# Revit family: HermanMiller_Seating_Verus_WorkChairUpholsteredBack
name_source: partatom
category: Furniture
revit_build: Autodesk Revit Architecture 2014 (Build: 20130308_1515(x64)
units: mm (PartAtom-declared; Revit-internal decimal feet)

## types (96) — shared parameters
Assembly Code = E2020200
Manufacturer = Herman Miller, Inc.
Package Qty = 1
URL = http://www.hermanmiller.com
zero-valued in all types: PosOpt

## per-type parameters (varying)
| type | Adj Arms | Arm Type | Arms | Description | Fixed Arms | Height Adjustable | Model | Sync |
| Low-Hgt Range Adj Wgt Act w/Tlt Lim Fully Adj Arms Adj Seat Depth | Yes | 2 | Yes | Wk Task Chr Verus Uphst Back Low-Hgt Range Adj Weight Activated w/Tlt Lim Fully Adj Arms Adj Seat Depth | No | Yes | PI1B215AA | No |
| Low-Hgt Range Adj Wgt Act w/Tlt Lim Fully Adj Arms Adj Seat Depth FR | Yes | 2 | Yes | Wk Task Chr Verus Uphst Back Low-Hgt Range Adj Weight Activated w/Tlt Lim Fully Adj Arms Adj Seat Depth FR | No | Yes | PI1B215AAFR | No |
| Low-Hgt Range Adj Wgt Act w/Tlt Lim Fully Adj Arms Fxd Seat Depth | Yes | 2 | Yes | Wk Task Chr Verus Uphst Back Low-Hgt Range Adj Weight Activated w/Tlt Lim Fully Adj Arms Fixed Seat Depth | No | Yes | PI1B215AF | No |
| Low-Hgt Range Adj Wgt Act w/Tlt Lim Fully Adj Arms Fxd Seat Depth FR | Yes | 2 | Yes | Wk Task Chr Verus Uphst Back Low-Hgt Range Adj Weight Activated w/Tlt Lim Fully Adj Arms Fixed Seat Depth FR | No | Yes | PI1B215AFFR | No |
| Low-Hgt Range Adj Wgt Act w/Tlt Lim Hgt Adj Arms Adj Seat Depth | Yes | 2 | Yes | Wk Task Chr Verus Uphst Back Low-Hgt Range Adj Weight Activated w/Tlt Lim Hgt Adj Arms Adj Seat Depth | No | Yes | PI1B215HA | No |
| Low-Hgt Range Adj Wgt Act w/Tlt Lim Hgt Adj Arms Adj Seat Depth FR | Yes | 2 | Yes | Wk Task Chr Verus Uphst Back Low-Hgt Range Adj Weight Activated w/Tlt Lim Hgt Adj Arms Adj Seat Depth FR | No | Yes | PI1B215HAFR | No |
| Low-Hgt Range Adj Wgt Act w/Tlt Lim Hgt Adj Arms Fxd Seat Depth | Yes | 2 | Yes | Wk Task Chr Verus Uphst Back Low-Hgt Range Adj Weight Activated w/Tlt Lim Hgt Adj Arms Fixed Seat Depth | No | Yes | PI1B215HF | No |
| Low-Hgt Range Adj Wgt Act w/Tlt Lim Hgt Adj Arms Fxd Seat Depth FR | Yes | 2 | Yes | Wk Task Chr Verus Uphst Back Low-Hgt Range Adj Weight Activated w/Tlt Lim Hgt Adj Arms Fixed Seat Depth FR | No | Yes | PI1B215HFFR | No |
| Low-Hgt Range Adj Wgt Act w/Tlt Lim No Arms Adj Seat Depth | No | 0 | No | Wk Task Chr Verus Uphst Back Low-Hgt Range Adj Weight Activated w/Tlt Lim No Arms Adj Seat Depth | No | Yes | PI1B215NA | No |
| Low-Hgt Range Adj Wgt Act w/Tlt Lim No Arms Adj Seat Depth FR | No | 0 | No | Wk Task Chr Verus Uphst Back Low-Hgt Range Adj Weight Activated w/Tlt Lim No Arms Adj Seat Depth FR | No | Yes | PI1B215NAFR | No |
| Low-Hgt Range Adj Wgt Act w/Tlt Lim No Arms Fxd Seat Depth | No | 0 | No | Wk Task Chr Verus Uphst Back Low-Hgt Range Adj Weight Activated w/Tlt Lim No Arms Fixed Seat Depth | No | Yes | PI1B215NF | No |
| Low-Hgt Range Adj Wgt Act w/Tlt Lim No Arms Fxd Seat Depth FR | No | 0 | No | Wk Task Chr Verus Uphst Back Low-Hgt Range Adj Weight Activated w/Tlt Lim No Arms Fixed Seat Depth FR | No | Yes | PI1B215NFFR | No |
| Low-Hgt Range Adj Wgt Act w/Tlt Lim Fxd Arms Adj Seat Depth | No | 1 | Yes | Wk Task Chr Verus Uphst Back Low-Hgt Range Adj Weight Activated w/Tlt Lim Fixed Arms Adj Seat Depth | Yes | Yes | PI1B215PA | No |
| Low-Hgt Range Adj Wgt Act w/Tlt Lim Fxd Arms Adj Seat Depth FR | No | 1 | Yes | Wk Task Chr Verus Uphst Back Low-Hgt Range Adj Weight Activated w/Tlt Lim Fixed Arms Adj Seat Depth FR | Yes | Yes | PI1B215PAFR | No |
| Low-Hgt Range Adj Wgt Act w/Tlt Lim Fxd Arms Fxd Seat Depth | No | 1 | Yes | Wk Task Chr Verus Uphst Back Low-Hgt Range Adj Weight Activated w/Tlt Lim Fixed Arms Fixed Seat Depth | Yes | Yes | PI1B215PF | No |
| Low-Hgt Range Adj Wgt Act w/Tlt Lim Fxd Arms Fxd Seat Depth FR | No | 1 | Yes | Wk Task Chr Verus Uphst Back Low-Hgt Range Adj Weight Activated w/Tlt Lim Fixed Arms Fixed Seat Depth FR | Yes | Yes | PI1B215PFFR | No |
| Low-Hgt Range Adj Sync w/Tlt Lim Fully Adj Arms Adj Seat Depth | Yes | 2 | Yes | Wk Task Chr Verus Uphst Back Low-Hgt Range Adj Synchronous w/Tlt Lim Fully Adj Arms Adj Seat Depth | No | No | PI1B216AA | Yes |
| Low-Hgt Range Adj Sync w/Tlt Lim Fully Adj Arms Adj Seat Depth FR | Yes | 2 | Yes | Wk Task Chr Verus Uphst Back Low-Hgt Range Adj Synchronous w/Tlt Lim Fully Adj Arms Adj Seat Depth FR | No | No | PI1B216AAFR | Yes |
| Low-Hgt Range Adj Sync w/Tlt Lim Fully Adj Arms Fxd Seat Depth | Yes | 2 | Yes | Wk Task Chr Verus Uphst Back Low-Hgt Range Adj Synchronous w/Tlt Lim Fully Adj Arms Fixed Seat Depth | No | No | PI1B216AF | Yes |
| Low-Hgt Range Adj Sync w/Tlt Lim Fully Adj Arms Fxd Seat Depth FR | Yes | 2 | Yes | Wk Task Chr Verus Uphst Back Low-Hgt Range Adj Synchronous w/Tlt Lim Fully Adj Arms Fixed Seat Depth FR | No | No | PI1B216AFFR | Yes |
| Low-Hgt Range Adj Sync w/Tlt Lim Hgt Adj Arms Adj Seat Depth | Yes | 2 | Yes | Wk Task Chr Verus Uphst Back Low-Hgt Range Adj Synchronous w/Tlt Lim Hgt Adj Arms Adj Seat Depth | No | No | PI1B216HA | Yes |
| Low-Hgt Range Adj Sync w/Tlt Lim Hgt Adj Arms Adj Seat Depth FR | Yes | 2 | Yes | Wk Task Chr Verus Uphst Back Low-Hgt Range Adj Synchronous w/Tlt Lim Hgt Adj Arms Adj Seat Depth FR | No | No | PI1B216HAFR | Yes |
| Low-Hgt Range Adj Sync w/Tlt Lim Hgt Adj Arms Fxd Seat Depth | Yes | 2 | Yes | Wk Task Chr Verus Uphst Back Low-Hgt Range Adj Synchronous w/Tlt Lim Hgt Adj Arms Fixed Seat Depth | No | No | PI1B216HF | Yes |
| Low-Hgt Range Adj Sync w/Tlt Lim Hgt Adj Arms Fxd Seat Depth FR | Yes | 2 | Yes | Wk Task Chr Verus Uphst Back Low-Hgt Range Adj Synchronous w/Tlt Lim Hgt Adj Arms Fixed Seat Depth FR | No | No | PI1B216HFFR | Yes |
| Low-Hgt Range Adj Sync w/Tlt Lim No Arms Adj Seat Depth | No | 0 | No | Wk Task Chr Verus Uphst Back Low-Hgt Range Adj Synchronous w/Tlt Lim No Arms Adj Seat Depth | No | No | PI1B216NA | Yes |
| Low-Hgt Range Adj Sync w/Tlt Lim No Arms Adj Seat Depth FR | No | 0 | No | Wk Task Chr Verus Uphst Back Low-Hgt Range Adj Synchronous w/Tlt Lim No Arms Adj Seat Depth FR | No | No | PI1B216NAFR | Yes |
| Low-Hgt Range Adj Sync w/Tlt Lim No Arms Fxd Seat Depth | No | 0 | No | Wk Task Chr Verus Uphst Back Low-Hgt Range Adj Synchronous w/Tlt Lim No Arms Fixed Seat Depth | No | No | PI1B216NF | Yes |
| Low-Hgt Range Adj Sync w/Tlt Lim No Arms Fxd Seat Depth FR | No | 0 | No | Wk Task Chr Verus Uphst Back Low-Hgt Range Adj Synchronous w/Tlt Lim No Arms Fixed Seat Depth FR | No | No | PI1B216NFFR | Yes |
| Low-Hgt Range Adj Sync w/Tlt Lim Fxd Arms Adj Seat Depth | No | 1 | Yes | Wk Task Chr Verus Uphst Back Low-Hgt Range Adj Synchronous w/Tlt Lim Fixed Arms Adj Seat Depth | Yes | No | PI1B216PA | Yes |
| Low-Hgt Range Adj Sync w/Tlt Lim Fxd Arms Adj Seat Depth FR | No | 1 | Yes | Wk Task Chr Verus Uphst Back Low-Hgt Range Adj Synchronous w/Tlt Lim Fixed Arms Adj Seat Depth FR | Yes | No | PI1B216PAFR | Yes |
| Low-Hgt Range Adj Sync w/Tlt Lim Fxd Arms Fxd Seat Depth | No | 1 | Yes | Wk Task Chr Verus Uphst Back Low-Hgt Range Adj Synchronous w/Tlt Lim Fixed Arms Fixed Seat Depth | Yes | No | PI1B216PF | Yes |
| Low-Hgt Range Adj Sync w/Tlt Lim Fxd Arms Fxd Seat Depth FR | No | 1 | Yes | Wk Task Chr Verus Uphst Back Low-Hgt Range Adj Synchronous w/Tlt Lim Fixed Arms Fixed Seat Depth FR | Yes | No | PI1B216PFFR | Yes |
| Low-Hgt Range Adj Sync w/Tlt Lim and Seat Angle Fully Adj Arms Adj Seat Depth | Yes | 2 | Yes | Wk Task Chr Verus Uphst Back Low-Hgt Range Adj Synchronous w/Tlt Lim and Seat Angle Fully Adj Arms Adj Seat Depth | No | No | PI1B217AA | Yes |
| Low-Hgt Range Adj Sync w/Tlt Lim and Seat Angle Fully Adj Arms Adj Seat Depth FR | Yes | 2 | Yes | Wk Task Chr Verus Uphst Back Low-Hgt Range Adj Synchronous w/Tlt Lim and Seat Angle Fully Adj Arms Adj Seat Depth FR | No | No | PI1B217AAFR | Yes |
| Low-Hgt Range Adj Sync w/Tlt Lim and Seat Angle Fully Adj Arms Fxd Seat Depth | Yes | 2 | Yes | Wk Task Chr Verus Uphst Back Low-Hgt Range Adj Synchronous w/Tlt Lim and Seat Angle Fully Adj Arms Fixed Seat Depth | No | No | PI1B217AF | Yes |
| Low-Hgt Range Adj Sync w/Tlt Lim and Seat Angle Fully Adj Arms Fxd Seat Depth FR | Yes | 2 | Yes | Wk Task Chr Verus Uphst Back Low-Hgt Range Adj Synchronous w/Tlt Lim and Seat Angle Fully Adj Arms Fixed Seat Depth FR | No | No | PI1B217AFFR | Yes |
| Low-Hgt Range Adj Sync w/Tlt Lim and Seat Angle Hgt Adj Arms Adj Seat Depth | Yes | 2 | Yes | Wk Task Chr Verus Uphst Back Low-Hgt Range Adj Synchronous w/Tlt Lim and Seat Angle Hgt Adj Arms Adj Seat Depth | No | No | PI1B217HA | Yes |
| Low-Hgt Range Adj Sync w/Tlt Lim and Seat Angle Hgt Adj Arms Adj Seat Depth FR | Yes | 2 | Yes | Wk Task Chr Verus Uphst Back Low-Hgt Range Adj Synchronous w/Tlt Lim and Seat Angle Hgt Adj Arms Adj Seat Depth FR | No | No | PI1B217HAFR | Yes |
| Low-Hgt Range Adj Sync w/Tlt Lim and Seat Angle Hgt Adj Arms Fxd Seat Depth | Yes | 2 | Yes | Wk Task Chr Verus Uphst Back Low-Hgt Range Adj Synchronous w/Tlt Lim and Seat Angle Hgt Adj Arms Fixed Seat Depth | No | No | PI1B217HF | Yes |
| Low-Hgt Range Adj Sync w/Tlt Lim and Seat Angle Hgt Adj Arms Fxd Seat Depth FR | Yes | 2 | Yes | Wk Task Chr Verus Uphst Back Low-Hgt Range Adj Synchronous w/Tlt Lim and Seat Angle Hgt Adj Arms Fixed Seat Depth FR | No | No | PI1B217HFFR | Yes |
| Low-Hgt Range Adj Sync w/Tlt Lim and Seat Angle No Arms Adj Seat Depth | No | 0 | No | Wk Task Chr Verus Uphst Back Low-Hgt Range Adj Synchronous w/Tlt Lim and Seat Angle No Arms Adj Seat Depth | No | No | PI1B217NA | Yes |
| Low-Hgt Range Adj Sync w/Tlt Lim and Seat Angle No Arms Adj Seat Depth FR | No | 0 | No | Wk Task Chr Verus Uphst Back Low-Hgt Range Adj Synchronous w/Tlt Lim and Seat Angle No Arms Adj Seat Depth FR | No | No | PI1B217NAFR | Yes |
| Low-Hgt Range Adj Sync w/Tlt Lim and Seat Angle No Arms Fxd Seat Depth | No | 0 | No | Wk Task Chr Verus Uphst Back Low-Hgt Range Adj Synchronous w/Tlt Lim and Seat Angle No Arms Fixed Seat Depth | No | No | PI1B217NF | Yes |
| Low-Hgt Range Adj Sync w/Tlt Lim and Seat Angle No Arms Fxd Seat Depth FR | No | 0 | No | Wk Task Chr Verus Uphst Back Low-Hgt Range Adj Synchronous w/Tlt Lim and Seat Angle No Arms Fixed Seat Depth FR | No | No | PI1B217NFFR | Yes |
| Low-Hgt Range Adj Sync w/Tlt Lim and Seat Angle Fxd Arms Adj Seat Depth | No | 1 | Yes | Wk Task Chr Verus Uphst Back Low-Hgt Range Adj Synchronous w/Tlt Lim and Seat Angle Fixed Arms Adj Seat Depth | Yes | No | PI1B217PA | Yes |
| Low-Hgt Range Adj Sync w/Tlt Lim and Seat Angle Fxd Arms Adj Seat Depth FR | No | 1 | Yes | Wk Task Chr Verus Uphst Back Low-Hgt Range Adj Synchronous w/Tlt Lim and Seat Angle Fixed Arms Adj Seat Depth FR | Yes | No | PI1B217PAFR | Yes |
| Low-Hgt Range Adj Sync w/Tlt Lim and Seat Angle Fxd Arms Fxd Seat Depth | No | 1 | Yes | Wk Task Chr Verus Uphst Back Low-Hgt Range Adj Synchronous w/Tlt Lim and Seat Angle Fixed Arms Fixed Seat Depth | Yes | No | PI1B217PF | Yes |
| Low-Hgt Range Adj Sync w/Tlt Lim and Seat Angle Fxd Arms Fxd Seat Depth FR | No | 1 | Yes | Wk Task Chr Verus Uphst Back Low-Hgt Range Adj Synchronous w/Tlt Lim and Seat Angle Fixed Arms Fixed Seat Depth FR | Yes | No | PI1B217PFFR | Yes |
| Std-Hgt Range Adj Wgt Act w/Tlt Lim Fully Adj Arms Adj Seat Depth | Yes | 2 | Yes | Wk Task Chr Verus Uphst Back Std-Hgt Range Adj Weight Activated w/Tlt Lim Fully Adj Arms Adj Seat Depth | No | Yes | PI1B225AA | No |
| Std-Hgt Range Adj Wgt Act w/Tlt Lim Fully Adj Arms Adj Seat Depth FR | Yes | 2 | Yes | Wk Task Chr Verus Uphst Back Std-Hgt Range Adj Weight Activated w/Tlt Lim Fully Adj Arms Adj Seat Depth FR | No | Yes | PI1B225AAFR | No |
| Std-Hgt Range Adj Wgt Act w/Tlt Lim Fully Adj Arms Fxd Seat Depth | Yes | 2 | Yes | Wk Task Chr Verus Uphst Back Std-Hgt Range Adj Weight Activated w/Tlt Lim Fully Adj Arms Fixed Seat Depth | No | Yes | PI1B225AF | No |
| Std-Hgt Range Adj Wgt Act w/Tlt Lim Fully Adj Arms Fxd Seat Depth FR | Yes | 2 | Yes | Wk Task Chr Verus Uphst Back Std-Hgt Range Adj Weight Activated w/Tlt Lim Fully Adj Arms Fixed Seat Depth FR | No | Yes | PI1B225AFFR | No |
| Std-Hgt Range Adj Wgt Act w/Tlt Lim Hgt Adj Arms Adj Seat Depth | Yes | 2 | Yes | Wk Task Chr Verus Uphst Back Std-Hgt Range Adj Weight Activated w/Tlt Lim Hgt Adj Arms Adj Seat Depth | No | Yes | PI1B225HA | No |
| Std-Hgt Range Adj Wgt Act w/Tlt Lim Hgt Adj Arms Adj Seat Depth FR | Yes | 2 | Yes | Wk Task Chr Verus Uphst Back Std-Hgt Range Adj Weight Activated w/Tlt Lim Hgt Adj Arms Adj Seat Depth FR | No | Yes | PI1B225HAFR | No |
| Std-Hgt Range Adj Wgt Act w/Tlt Lim Hgt Adj Arms Fxd Seat Depth | Yes | 2 | Yes | Wk Task Chr Verus Uphst Back Std-Hgt Range Adj Weight Activated w/Tlt Lim Hgt Adj Arms Fixed Seat Depth | No | Yes | PI1B225HF | No |
| Std-Hgt Range Adj Wgt Act w/Tlt Lim Hgt Adj Arms Fxd Seat Depth FR | Yes | 2 | Yes | Wk Task Chr Verus Uphst Back Std-Hgt Range Adj Weight Activated w/Tlt Lim Hgt Adj Arms Fixed Seat Depth FR | No | Yes | PI1B225HFFR | No |
| Std-Hgt Range Adj Wgt Act w/Tlt Lim No Arms Adj Seat Depth | No | 0 | No | Wk Task Chr Verus Uphst Back Std-Hgt Range Adj Weight Activated w/Tlt Lim No Arms Adj Seat Depth | No | Yes | PI1B225NA | No |
| Std-Hgt Range Adj Wgt Act w/Tlt Lim No Arms Adj Seat Depth FR | No | 0 | No | Wk Task Chr Verus Uphst Back Std-Hgt Range Adj Weight Activated w/Tlt Lim No Arms Adj Seat Depth FR | No | Yes | PI1B225NAFR | No |
| Std-Hgt Range Adj Wgt Act w/Tlt Lim No Arms Fxd Seat Depth | No | 0 | No | Wk Task Chr Verus Uphst Back Std-Hgt Range Adj Weight Activated w/Tlt Lim No Arms Fixed Seat Depth | No | Yes | PI1B225NF | No |
| Std-Hgt Range Adj Wgt Act w/Tlt Lim No Arms Fxd Seat Depth FR | No | 0 | No | Wk Task Chr Verus Uphst Back Std-Hgt Range Adj Weight Activated w/Tlt Lim No Arms Fixed Seat Depth FR | No | Yes | PI1B225NFFR | No |
| Std-Hgt Range Adj Wgt Act w/Tlt Lim Fxd Arms Adj Seat Depth | No | 1 | Yes | Wk Task Chr Verus Uphst Back Std-Hgt Range Adj Weight Activated w/Tlt Lim Fixed Arms Adj Seat Depth | Yes | Yes | PI1B225PA | No |
| Std-Hgt Range Adj Wgt Act w/Tlt Lim Fxd Arms Adj Seat Depth FR | No | 1 | Yes | Wk Task Chr Verus Uphst Back Std-Hgt Range Adj Weight Activated w/Tlt Lim Fixed Arms Adj Seat Depth FR | Yes | Yes | PI1B225PAFR | No |
| Std-Hgt Range Adj Wgt Act w/Tlt Lim Fxd Arms Fxd Seat Depth | No | 1 | Yes | Wk Task Chr Verus Uphst Back Std-Hgt Range Adj Weight Activated w/Tlt Lim Fixed Arms Fixed Seat Depth | Yes | Yes | PI1B225PF | No |
| Std-Hgt Range Adj Wgt Act w/Tlt Lim Fxd Arms Fxd Seat Depth FR | No | 1 | Yes | Wk Task Chr Verus Uphst Back Std-Hgt Range Adj Weight Activated w/Tlt Lim Fixed Arms Fixed Seat Depth FR | Yes | Yes | PI1B225PFFR | No |
| Std-Hgt Range Adj Sync w/Tlt Lim Fully Adj Arms Adj Seat Depth | Yes | 2 | Yes | Wk Task Chr Verus Uphst Back Std-Hgt Range Adj Synchronous w/Tlt Lim Fully Adj Arms Adj Seat Depth | No | No | PI1B226AA | Yes |
| Std-Hgt Range Adj Sync w/Tlt Lim Fully Adj Arms Adj Seat Depth FR | Yes | 2 | Yes | Wk Task Chr Verus Uphst Back Std-Hgt Range Adj Synchronous w/Tlt Lim Fully Adj Arms Adj Seat Depth FR | No | No | PI1B226AAFR | Yes |
| Std-Hgt Range Adj Sync w/Tlt Lim Fully Adj Arms Fxd Seat Depth | Yes | 2 | Yes | Wk Task Chr Verus Uphst Back Std-Hgt Range Adj Synchronous w/Tlt Lim Fully Adj Arms Fixed Seat Depth | No | No | PI1B226AF | Yes |
| Std-Hgt Range Adj Sync w/Tlt Lim Fully Adj Arms Fxd Seat Depth FR | Yes | 2 | Yes | Wk Task Chr Verus Uphst Back Std-Hgt Range Adj Synchronous w/Tlt Lim Fully Adj Arms Fixed Seat Depth FR | No | No | PI1B226AFFR | Yes |
| Std-Hgt Range Adj Sync w/Tlt Lim Hgt Adj Arms Adj Seat Depth | Yes | 2 | Yes | Wk Task Chr Verus Uphst Back Std-Hgt Range Adj Synchronous w/Tlt Lim Hgt Adj Arms Adj Seat Depth | No | No | PI1B226HA | Yes |
| Std-Hgt Range Adj Sync w/Tlt Lim Hgt Adj Arms Adj Seat Depth FR | Yes | 2 | Yes | Wk Task Chr Verus Uphst Back Std-Hgt Range Adj Synchronous w/Tlt Lim Hgt Adj Arms Adj Seat Depth FR | No | No | PI1B226HAFR | Yes |
| Std-Hgt Range Adj Sync w/Tlt Lim Hgt Adj Arms Fxd Seat Depth | Yes | 2 | Yes | Wk Task Chr Verus Uphst Back Std-Hgt Range Adj Synchronous w/Tlt Lim Hgt Adj Arms Fixed Seat Depth | No | No | PI1B226HF | Yes |
| Std-Hgt Range Adj Sync w/Tlt Lim Hgt Adj Arms Fxd Seat Depth FR | Yes | 2 | Yes | Wk Task Chr Verus Uphst Back Std-Hgt Range Adj Synchronous w/Tlt Lim Hgt Adj Arms Fixed Seat Depth FR | No | No | PI1B226HFFR | Yes |
| Std-Hgt Range Adj Sync w/Tlt Lim No Arms Adj Seat Depth | No | 0 | No | Wk Task Chr Verus Uphst Back Std-Hgt Range Adj Synchronous w/Tlt Lim No Arms Adj Seat Depth | No | No | PI1B226NA | Yes |
| Std-Hgt Range Adj Sync w/Tlt Lim No Arms Adj Seat Depth FR | No | 0 | No | Wk Task Chr Verus Uphst Back Std-Hgt Range Adj Synchronous w/Tlt Lim No Arms Adj Seat Depth FR | No | No | PI1B226NAFR | Yes |
| Std-Hgt Range Adj Sync w/Tlt Lim No Arms Fxd Seat Depth | No | 0 | No | Wk Task Chr Verus Uphst Back Std-Hgt Range Adj Synchronous w/Tlt Lim No Arms Fixed Seat Depth | No | No | PI1B226NF | Yes |
| Std-Hgt Range Adj Sync w/Tlt Lim No Arms Fxd Seat Depth FR | No | 0 | No | Wk Task Chr Verus Uphst Back Std-Hgt Range Adj Synchronous w/Tlt Lim No Arms Fixed Seat Depth FR | No | No | PI1B226NFFR | Yes |
| Std-Hgt Range Adj Sync w/Tlt Lim Fxd Arms Adj Seat Depth | No | 1 | Yes | Wk Task Chr Verus Uphst Back Std-Hgt Range Adj Synchronous w/Tlt Lim Fixed Arms Adj Seat Depth | Yes | No | PI1B226PA | Yes |
| Std-Hgt Range Adj Sync w/Tlt Lim Fxd Arms Adj Seat Depth FR | No | 1 | Yes | Wk Task Chr Verus Uphst Back Std-Hgt Range Adj Synchronous w/Tlt Lim Fixed Arms Adj Seat Depth FR | Yes | No | PI1B226PAFR | Yes |
| Std-Hgt Range Adj Sync w/Tlt Lim Fxd Arms Fxd Seat Depth | No | 1 | Yes | Wk Task Chr Verus Uphst Back Std-Hgt Range Adj Synchronous w/Tlt Lim Fixed Arms Fixed Seat Depth | Yes | No | PI1B226PF | Yes |
| Std-Hgt Range Adj Sync w/Tlt Lim Fxd Arms Fxd Seat Depth FR | No | 1 | Yes | Wk Task Chr Verus Uphst Back Std-Hgt Range Adj Synchronous w/Tlt Lim Fixed Arms Fixed Seat Depth FR | Yes | No | PI1B226PFFR | Yes |
| Std-Hgt Range Adj Sync w/Tlt Lim and Seat Angle Fully Adj Arms Adj Seat Depth | Yes | 2 | Yes | Wk Task Chr Verus Uphst Back Std-Hgt Range Adj Synchronous w/Tlt Lim and Seat Angle Fully Adj Arms Adj Seat Depth | No | No | PI1B227AA | Yes |
| Std-Hgt Range Adj Sync w/Tlt Lim and Seat Angle Fully Adj Arms Adj Seat Depth FR | Yes | 2 | Yes | Wk Task Chr Verus Uphst Back Std-Hgt Range Adj Synchronous w/Tlt Lim and Seat Angle Fully Adj Arms Adj Seat Depth FR | No | No | PI1B227AAFR | Yes |
| Std-Hgt Range Adj Sync w/Tlt Lim and Seat Angle Fully Adj Arms Fxd Seat Depth | Yes | 2 | Yes | Wk Task Chr Verus Uphst Back Std-Hgt Range Adj Synchronous w/Tlt Lim and Seat Angle Fully Adj Arms Fixed Seat Depth | No | No | PI1B227AF | Yes |
| Std-Hgt Range Adj Sync w/Tlt Lim and Seat Angle Fully Adj Arms Fxd Seat Depth FR | Yes | 2 | Yes | Wk Task Chr Verus Uphst Back Std-Hgt Range Adj Synchronous w/Tlt Lim and Seat Angle Fully Adj Arms Fixed Seat Depth FR | No | No | PI1B227AFFR | Yes |
| Std-Hgt Range Adj Sync w/Tlt Lim and Seat Angle Hgt Adj Arms Adj Seat Depth | Yes | 2 | Yes | Wk Task Chr Verus Uphst Back Std-Hgt Range Adj Synchronous w/Tlt Lim and Seat Angle Hgt Adj Arms Adj Seat Depth | No | No | PI1B227HA | Yes |
| Std-Hgt Range Adj Sync w/Tlt Lim and Seat Angle Hgt Adj Arms Adj Seat Depth FR | Yes | 2 | Yes | Wk Task Chr Verus Uphst Back Std-Hgt Range Adj Synchronous w/Tlt Lim and Seat Angle Hgt Adj Arms Adj Seat Depth FR | No | No | PI1B227HAFR | Yes |
| Std-Hgt Range Adj Sync w/Tlt Lim and Seat Angle Hgt Adj Arms Fxd Seat Depth | Yes | 2 | Yes | Wk Task Chr Verus Uphst Back Std-Hgt Range Adj Synchronous w/Tlt Lim and Seat Angle Hgt Adj Arms Fixed Seat Depth | No | No | PI1B227HF | Yes |
| Std-Hgt Range Adj Sync w/Tlt Lim and Seat Angle Hgt Adj Arms Fxd Seat Depth FR | Yes | 2 | Yes | Wk Task Chr Verus Uphst Back Std-Hgt Range Adj Synchronous w/Tlt Lim and Seat Angle Hgt Adj Arms Fixed Seat Depth FR | No | No | PI1B227HFFR | Yes |
| Std-Hgt Range Adj Sync w/Tlt Lim and Seat Angle No Arms Adj Seat Depth | No | 0 | No | Wk Task Chr Verus Uphst Back Std-Hgt Range Adj Synchronous w/Tlt Lim and Seat Angle No Arms Adj Seat Depth | No | No | PI1B227NA | Yes |
| Std-Hgt Range Adj Sync w/Tlt Lim and Seat Angle No Arms Adj Seat Depth FR | No | 0 | No | Wk Task Chr Verus Uphst Back Std-Hgt Range Adj Synchronous w/Tlt Lim and Seat Angle No Arms Adj Seat Depth FR | No | No | PI1B227NAFR | Yes |
| Std-Hgt Range Adj Sync w/Tlt Lim and Seat Angle No Arms Fxd Seat Depth | No | 0 | No | Wk Task Chr Verus Uphst Back Std-Hgt Range Adj Synchronous w/Tlt Lim and Seat Angle No Arms Fixed Seat Depth | No | No | PI1B227NF | Yes |
| Std-Hgt Range Adj Sync w/Tlt Lim and Seat Angle No Arms Fxd Seat Depth FR | No | 0 | No | Wk Task Chr Verus Uphst Back Std-Hgt Range Adj Synchronous w/Tlt Lim and Seat Angle No Arms Fixed Seat Depth FR | No | No | PI1B227NFFR | Yes |
| Std-Hgt Range Adj Sync w/Tlt Lim and Seat Angle Fxd Arms Adj Seat Depth | No | 1 | Yes | Wk Task Chr Verus Uphst Back Std-Hgt Range Adj Synchronous w/Tlt Lim and Seat Angle Fixed Arms Adj Seat Depth | Yes | No | PI1B227PA | Yes |
| Std-Hgt Range Adj Sync w/Tlt Lim and Seat Angle Fxd Arms Adj Seat Depth FR | No | 1 | Yes | Wk Task Chr Verus Uphst Back Std-Hgt Range Adj Synchronous w/Tlt Lim and Seat Angle Fixed Arms Adj Seat Depth FR | Yes | No | PI1B227PAFR | Yes |
| Std-Hgt Range Adj Sync w/Tlt Lim and Seat Angle Fxd Arms Fxd Seat Depth | No | 1 | Yes | Wk Task Chr Verus Uphst Back Std-Hgt Range Adj Synchronous w/Tlt Lim and Seat Angle Fixed Arms Fixed Seat Depth | Yes | No | PI1B227PF | Yes |
| Std-Hgt Range Adj Sync w/Tlt Lim and Seat Angle Fxd Arms Fxd Seat Depth FR | No | 1 | Yes | Wk Task Chr Verus Uphst Back Std-Hgt Range Adj Synchronous w/Tlt Lim and Seat Angle Fixed Arms Fixed Seat Depth FR | Yes | No | PI1B227PFFR | Yes |

## geometry (parser evidence)
native form markers: Blend x13, Sweep x10
no freeform markers — native parametric forms only
